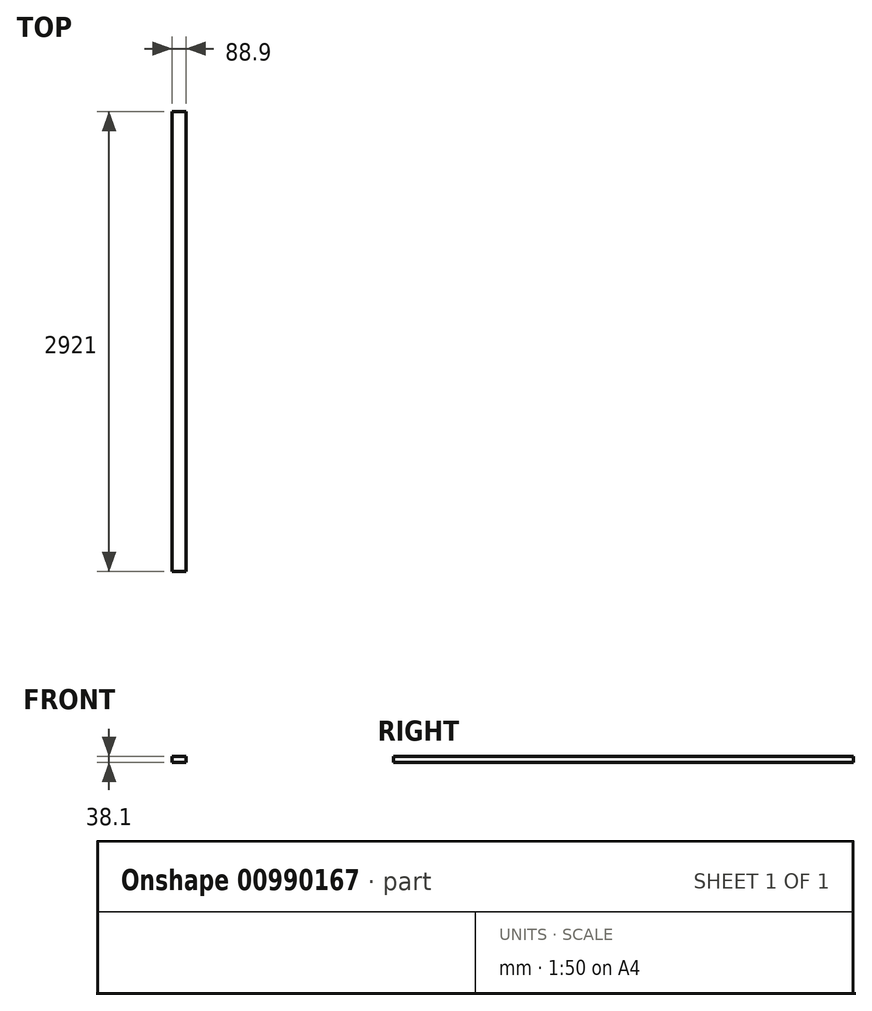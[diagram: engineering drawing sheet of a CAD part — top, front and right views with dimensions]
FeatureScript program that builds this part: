
annotation { "Feature Type Name" : "Feature", "Feature Type Description" : "" }
export const myFeature = defineFeature(function(context is Context, id is Id, definition is map)
    precondition{}
    {
        {
            assignVariable(context, id + "F0", {"name" : "w", "anyValue" : 38.1 * mm});
        }
        {
            var Q0;
            Q0=qCreatedBy(makeId("Top.planeOp"),FACE);
            var sketch = newSketch(context, id + "F1", { "sketchPlane" : qUnion([Q0])});
            skLineSegment(sketch, "E0.bottom", {"start": v(44.45, 1460.5) * mm, "end": v(-44.45, 1460.5) * mm});
            skLineSegment(sketch, "E0.top", {"start": v(44.45, -1460.5) * mm, "end": v(-44.45, -1460.5) * mm});
            skLineSegment(sketch, "E0.left", {"start": v(44.45, 1460.5) * mm, "end": v(44.45, -1460.5) * mm});
            skLineSegment(sketch, "E0.right", {"start": v(-44.45, 1460.5) * mm, "end": v(-44.45, -1460.5) * mm});
            skPoint(sketch, "E0.middle", {"position": v(0, 0) * mm});
            skSolve(sketch);
        }
        {
            var Q0;
            Q0=qSketchRegion(id+"F1",true);
            extrude(context, id + "F2", {"entities" : qUnion([Q0]), "depth" : getVariable(context, 'w'), "offsetDistance" : 25.4 * mm});
        }
    });
